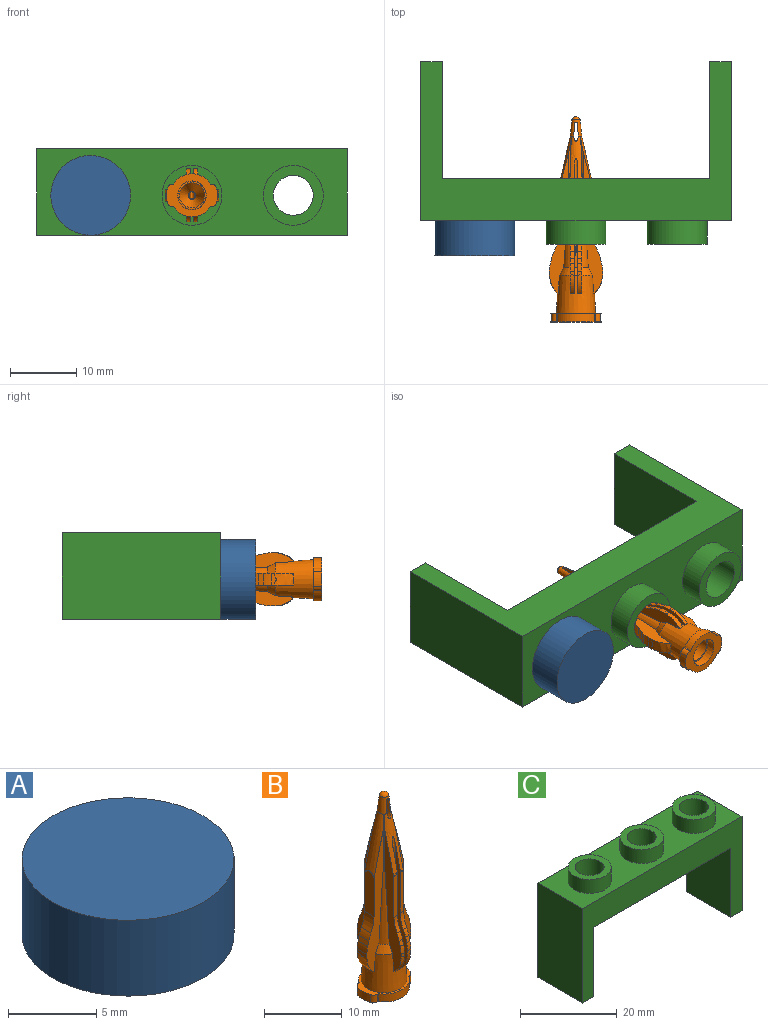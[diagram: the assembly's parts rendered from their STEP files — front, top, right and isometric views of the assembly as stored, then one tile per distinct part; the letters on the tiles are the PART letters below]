
ASSEMBLY  parts=3 mates=2
PART A: 3 faces, bbox 12x12x5.3 mm
  f0: cylinder r=6mm len=12mm, axis (0,0,-1), area 197.9mm2, adj f1,f2
  f1: plane 12x12mm, normal (0,0,1), area 113.1mm2, adj f0
  f2: plane 12x12mm, normal (0,0,-1), area 113.1mm2, adj f0
PART B: 130 faces, bbox 8.4x8.4x31.3 mm
  f0: cone r=0.52mm half-angle=51deg, axis (0,0,-1), area 0mm2, adj f12,f128
  f1: cone r=0.38mm half-angle=6deg, axis (0,0,-1), area 9.4mm2, adj f2,f5,f8,f34,f114,f115,f116,f117
  f2: cone r=3.2mm half-angle=12.5deg, axis (0,0,-1), area 12.4mm2, adj f1,f3,f4,f46,f47,f79,f82,f85
  f3: plane 19.1x2.13mm, normal (-1,-0.02,0), area 16.3mm2, adj f2,f55,f56,f57,f58,f82,f83,f95
  f4: plane 19.1x2.13mm, normal (1,-0.02,0), area 16.3mm2, adj f2,f51,f52,f53,f54,f81,f82,f95
  f5: cone r=0.87mm half-angle=12.5deg, axis (0,0,-1), area 12.4mm2, adj f1,f6,f7,f49,f50,f67,f70,f97
  f6: plane 19.1x2.13mm, normal (1,0.02,0), area 16.3mm2, adj f5,f91,f92,f93,f94,f95,f96,f97
  f7: plane 19.1x2.13mm, normal (-1,0.02,0), area 16.3mm2, adj f5,f86,f87,f88,f89,f90,f95,f97
  f8: cone r=0.87mm half-angle=12.6deg, axis (0,0,-1), area 16.6mm2, adj f1,f9,f39,f43,f72,f123
  f9: plane 21.7x3.25mm, normal (0,-1,0), area 26.6mm2, adj f8,f40,f41,f42,f43,f44,f75,f76
  f10: cone r=0.6mm half-angle=24.1deg, axis (0,0,-1), area 25mm2, adj f11,f15
  f11: cylinder r=0.6mm len=13.21mm, axis (0,0,1), area 49.8mm2, adj f10,f12
  f12: cone r=0.52mm half-angle=1deg, axis (0,0,-1), area 16.2mm2, adj f0,f11,f13,f125,f126
  f13: cone r=0.52mm half-angle=51deg, axis (0,0,-1), area 0mm2, adj f12,f127
  f14: plane 4.24x4.24mm, normal (0,0,-1), area 2.8mm2, adj f15,f28
  f15: cylinder r=1.9mm len=5.75mm, axis (0,0,1), area 68.6mm2, adj f10,f14
  f16: plane 1.25x0.12mm, normal (0,-1,0), area 0.1mm2, adj f17,f27,f29,f59
  f17: cylinder r=0.8mm len=1.25mm, axis (0,0,-1), area 1.3mm2, adj f16,f18,f27,f59
  f18: cylinder r=3.82mm len=2.28mm, axis (0,0,-1), area 2.9mm2, adj f17,f19,f27,f59
  f19: cylinder r=0.8mm len=1.25mm, axis (0,0,-1), area 1.3mm2, adj f18,f20,f27,f59
  f20: plane 1.25x0.12mm, normal (0,1,0), area 0.1mm2, adj f19,f21,f27,f59
  f21: cylinder r=3.25mm len=5.54mm, axis (0,0,1), area 8.3mm2, adj f20,f22,f27,f59
  f22: plane 1.25x0.12mm, normal (0,1,0), area 0.1mm2, adj f21,f23,f27,f59
  f23: cylinder r=0.8mm len=1.25mm, axis (0,0,-1), area 1.3mm2, adj f22,f24,f27,f59
  f24: cylinder r=3.82mm len=2.28mm, axis (0,0,-1), area 2.9mm2, adj f23,f25,f27,f59
  f25: cylinder r=0.8mm len=1.25mm, axis (0,0,-1), area 1.3mm2, adj f24,f26,f27,f59
  f26: plane 1.25x0.12mm, normal (0,-1,0), area 0.1mm2, adj f25,f27,f29,f59
  f27: plane 7.65x6.5mm, normal (0,0,-1), area 22.3mm2, adj f16,f17,f18,f19,f20,f21,f22,f23
  f28: cone r=1.9mm half-angle=2.2deg, axis (0,0,-1), area 16.9mm2, adj f14,f27
  f29: cylinder r=3.25mm len=5.54mm, axis (0,0,1), area 8.3mm2, adj f16,f26,f27,f59
  f30: plane 8.53x0.39mm, normal (-0.64,-0.77,0), area 1.6mm2, adj f34,f61,f114
  f31: plane 1.77x0.74mm, normal (0.97,0,0.24), area 1.3mm2, adj f61,f65,f110,f111
  f32: cylinder r=5mm len=2.29mm, axis (0,1,0), area 4.2mm2, adj f33,f61,f65,f111
  f33: plane 6.76x1.77mm, normal (1,0,0), area 11.5mm2, adj f32,f61,f65,f122
  f34: cone r=3.2mm half-angle=12.6deg, axis (0,0,-1), area 16.6mm2, adj f1,f30,f35,f61,f65,f122
  f35: plane 8.53x0.39mm, normal (-0.64,0.77,0), area 1.6mm2, adj f34,f65,f117
  f36: plane 1.77x0.73mm, normal (1,0,0), area 1mm2, adj f61,f63,f65,f110
  f37: plane 0.04x0.02mm, normal (0,-0.93,-0.37), area 0mm2, adj f66,f67,f117
  f38: plane 0.04x0.02mm, normal (0,-0.93,-0.37), area 0mm2, adj f70,f71,f116
  f39: plane 8.53x0.39mm, normal (0.64,0.77,0), area 1.6mm2, adj f8,f72,f116
  f40: plane 1.77x0.74mm, normal (-0.97,0,0.24), area 1.3mm2, adj f9,f72,f108,f109
  f41: cylinder r=5mm len=2.29mm, axis (0,-1,0), area 4.2mm2, adj f9,f42,f72,f109
  f42: plane 6.76x1.77mm, normal (-1,0,0), area 11.5mm2, adj f9,f41,f72,f123
  f43: plane 8.53x0.39mm, normal (0.64,-0.77,0), area 1.6mm2, adj f8,f9,f115
  f44: plane 1.77x0.73mm, normal (-1,0,0), area 1mm2, adj f9,f72,f75,f108
  f45: plane 0.04x0.02mm, normal (0,0.93,-0.37), area 0mm2, adj f78,f79,f115
  f46: plane 8.53x0.39mm, normal (-0.77,0.64,0), area 1.6mm2, adj f2,f79,f115
  f47: plane 8.53x0.39mm, normal (0.77,0.64,0), area 1.6mm2, adj f2,f85,f114
  f48: plane 0.04x0.02mm, normal (0,0.93,-0.37), area 0mm2, adj f60,f85,f114
  f49: plane 8.53x0.39mm, normal (0.77,-0.64,0), area 1.6mm2, adj f5,f67,f117
  f50: plane 8.53x0.39mm, normal (-0.77,-0.64,0), area 1.6mm2, adj f5,f70,f116
  f51: plane 0.67x0.6mm, normal (0,-1,0), area 0.3mm2, adj f4,f79,f81,f102
  f52: plane 0.74x0.61mm, normal (0,-0.97,0.24), area 0.5mm2, adj f4,f79,f102,f103
  f53: cylinder r=5mm len=2.29mm, axis (1,0,0), area 1.5mm2, adj f4,f54,f79,f103
  f54: plane 6.68x0.62mm, normal (0,-1,0), area 4mm2, adj f4,f53,f79,f119
  f55: plane 6.68x0.62mm, normal (0,-1,0), area 4mm2, adj f3,f56,f85,f118
  f56: cylinder r=5mm len=2.29mm, axis (1,0,0), area 1.5mm2, adj f3,f55,f85,f106
  f57: plane 0.74x0.61mm, normal (0,-0.97,0.24), area 0.5mm2, adj f3,f85,f106,f107
  f58: plane 0.67x0.6mm, normal (0,-1,0), area 0.3mm2, adj f3,f83,f85,f107
  f59: plane 7.65x6.5mm, normal (0,0,1), area 9.7mm2, adj f16,f17,f18,f19,f20,f21,f22,f23
  f60: cone r=2.63mm half-angle=25.5deg, axis (0,0,-1), area 2.5mm2, adj f48,f61,f85,f95,f114
  f61: plane 21.7x3.25mm, normal (0,-1,0), area 26.7mm2, adj f30,f31,f32,f33,f34,f36,f60,f62
  f62: plane 0.52x0.24mm, normal (-0.98,0,-0.18), area 0mm2, adj f61,f63,f95
  f63: bspline ~4.99x3.09mm, area 5.6mm2, adj f36,f61,f62,f64,f65,f95
  f64: plane 0.52x0.24mm, normal (-0.98,0,-0.18), area 0mm2, adj f63,f65,f95
  f65: plane 21.7x3.25mm, normal (0,1,0), area 26.7mm2, adj f31,f32,f33,f34,f35,f36,f63,f64
  f66: cone r=2.63mm half-angle=25.5deg, axis (0,0,-1), area 2.5mm2, adj f37,f65,f67,f95,f117
  f67: plane 21.42x2.98mm, normal (1,0,0), area 26.7mm2, adj f5,f37,f49,f66,f68,f86,f87,f88
  f68: plane 1.1x0.27mm, normal (0,-0.99,-0.12), area 0.1mm2, adj f67,f86,f95
  f69: plane 1.1x0.27mm, normal (0,-0.99,-0.12), area 0.1mm2, adj f70,f95,f96
  f70: plane 21.42x2.98mm, normal (-1,0,0), area 26.7mm2, adj f5,f38,f50,f69,f71,f91,f92,f93
  f71: cone r=2.63mm half-angle=25.5deg, axis (0,0,-1), area 2.5mm2, adj f38,f70,f72,f95,f116
  f72: plane 21.7x3.25mm, normal (0,1,0), area 26.6mm2, adj f8,f39,f40,f41,f42,f44,f71,f73
  f73: plane 0.06x0.04mm, normal (0.88,0,-0.47), area 0mm2, adj f72,f74,f95
  f74: plane 2.29x0.21mm, normal (1,0,-0.08), area 0.3mm2, adj f72,f73,f75,f95
  f75: bspline ~4.99x3.09mm, area 5.6mm2, adj f9,f44,f72,f74,f76,f95
  f76: plane 2.29x0.21mm, normal (1,0,-0.08), area 0.3mm2, adj f9,f75,f77,f95
  f77: plane 0.06x0.04mm, normal (0.88,0,-0.47), area 0mm2, adj f9,f76,f95
  f78: cone r=2.63mm half-angle=25.5deg, axis (0,0,-1), area 2.5mm2, adj f9,f45,f79,f95,f115
  f79: plane 21.42x2.98mm, normal (-1,0,0), area 26.7mm2, adj f2,f45,f46,f51,f52,f53,f54,f78
  f80: plane 1.1x0.27mm, normal (0,0.99,-0.12), area 0.1mm2, adj f79,f81,f95
  f81: bspline ~3.08x2.76mm, area 2mm2, adj f4,f51,f79,f80,f95
  f82: bspline ~23.75x0.91mm, area 11.2mm2, adj f2,f3,f4,f99,f112
  f83: bspline ~3.08x2.76mm, area 2mm2, adj f3,f58,f84,f85,f95
  f84: plane 1.1x0.27mm, normal (0,0.99,-0.12), area 0.1mm2, adj f83,f85,f95
  f85: plane 21.42x2.98mm, normal (1,0,0), area 26.7mm2, adj f2,f47,f48,f55,f56,f57,f58,f60
  f86: bspline ~3.08x2.76mm, area 2mm2, adj f7,f67,f68,f87,f95
  f87: plane 0.67x0.6mm, normal (0,1,0), area 0.3mm2, adj f7,f67,f86,f104
  f88: plane 0.74x0.61mm, normal (0,0.97,0.24), area 0.5mm2, adj f7,f67,f104,f105
  f89: cylinder r=5mm len=2.29mm, axis (-1,0,0), area 1.5mm2, adj f7,f67,f90,f105
  f90: plane 6.68x0.62mm, normal (0,1,0), area 4mm2, adj f7,f67,f89,f121
  f91: plane 6.68x0.62mm, normal (0,1,0), area 4mm2, adj f6,f70,f92,f120
  f92: cylinder r=5mm len=2.29mm, axis (-1,0,0), area 1.5mm2, adj f6,f70,f91,f101
  f93: plane 0.74x0.61mm, normal (0,0.97,0.24), area 0.5mm2, adj f6,f70,f100,f101
  f94: plane 0.67x0.6mm, normal (0,1,0), area 0.3mm2, adj f6,f70,f96,f100
  f95: cone r=2.63mm half-angle=3.2deg, axis (0,0,-1), area 85.1mm2, adj f3,f4,f6,f7,f9,f59,f60,f61
  f96: bspline ~3.08x2.76mm, area 2mm2, adj f6,f69,f70,f94,f95
  f97: bspline ~23.75x0.91mm, area 11.2mm2, adj f5,f6,f7,f98,f113
  f98: cone r=1.14mm half-angle=26.4deg, axis (0,0,-1), area 0.7mm2, adj f6,f7,f95,f97,f113
  f99: cone r=1.14mm half-angle=26.4deg, axis (0,0,-1), area 0.7mm2, adj f3,f4,f82,f95,f112
  f100: cylinder r=5mm len=1.21mm, axis (-1,0,0), area 0.7mm2, adj f6,f70,f93,f94
  f101: cylinder r=5mm len=1.08mm, axis (-1,0,0), area 0.7mm2, adj f6,f70,f92,f93
  f102: cylinder r=5mm len=1.21mm, axis (1,0,0), area 0.7mm2, adj f4,f51,f52,f79
  f103: cylinder r=5mm len=1.08mm, axis (1,0,0), area 0.7mm2, adj f4,f52,f53,f79
  f104: cylinder r=5mm len=1.21mm, axis (-1,0,0), area 0.7mm2, adj f7,f67,f87,f88
  f105: cylinder r=5mm len=1.08mm, axis (-1,0,0), area 0.7mm2, adj f7,f67,f88,f89
  f106: cylinder r=5mm len=1.08mm, axis (1,0,0), area 0.7mm2, adj f3,f56,f57,f85
  f107: cylinder r=5mm len=1.21mm, axis (1,0,0), area 0.7mm2, adj f3,f57,f58,f85
  f108: cylinder r=5mm len=1.77mm, axis (0,1,0), area 2.2mm2, adj f9,f40,f44,f72
  f109: cylinder r=5mm len=1.77mm, axis (0,-1,0), area 2.1mm2, adj f9,f40,f41,f72
  f110: cylinder r=5mm len=1.77mm, axis (0,1,0), area 2.2mm2, adj f31,f36,f61,f65
  f111: cylinder r=5mm len=1.77mm, axis (0,1,0), area 2.1mm2, adj f31,f32,f61,f65
  f112: cone r=0.87mm half-angle=3.4deg, axis (0,0,-1), area 1.2mm2, adj f82,f99
  f113: cone r=0.87mm half-angle=3.4deg, axis (0,0,-1), area 1.2mm2, adj f97,f98
  f114: cone r=0.87mm half-angle=3.4deg, axis (0,0,-1), area 10.9mm2, adj f1,f30,f47,f48,f60,f61,f85
  f115: cone r=0.87mm half-angle=3.4deg, axis (0,0,-1), area 10.9mm2, adj f1,f9,f43,f45,f46,f78,f79
  f116: cone r=0.87mm half-angle=3.4deg, axis (0,0,-1), area 10.9mm2, adj f1,f38,f39,f50,f70,f71,f72
  f117: cone r=0.87mm half-angle=3.4deg, axis (0,0,-1), area 10.9mm2, adj f1,f35,f37,f49,f65,f66,f67
  f118: bspline ~0.9x0.89mm, area 0.1mm2, adj f2,f3,f55,f85
  f119: bspline ~0.9x0.89mm, area 0.1mm2, adj f2,f4,f54,f79
  f120: bspline ~0.9x0.89mm, area 0.1mm2, adj f5,f6,f70,f91
  f121: bspline ~0.94x0.93mm, area 0.1mm2, adj f5,f7,f67,f90
  f122: bspline ~2.25x1mm, area 0.2mm2, adj f33,f34,f61,f65
  f123: bspline ~2.25x1mm, area 0.2mm2, adj f8,f9,f42,f72
  f124: sphere r=0.66mm, area 1.7mm2, adj f1
  f125: extruded ~0.8x0.73mm, area 1mm2, adj f5,f12,f127,f128
  f126: extruded ~0.8x0.73mm, area 1mm2, adj f2,f12,f127,f128
  f127: plane 2.36x1.99mm, normal (0.99,0,-0.1), area 2.7mm2, adj f1,f13,f125,f126,f129
  f128: plane 2.36x1.99mm, normal (-0.99,0,-0.1), area 2.7mm2, adj f0,f1,f125,f126,f129
  f129: cylinder r=0.17mm len=1.29mm, axis (0,-1,0), area 0.6mm2, adj f1,f127,f128
PART C: 19 faces, bbox 46.7x13x27.4 mm
  f0: plane 46.75x23.89mm, normal (0,1,0), area 412mm2, adj f1,f2,f3,f4,f5,f7,f17,f18
  f1: plane 23.89x13mm, normal (-1,0,0), area 310.6mm2, adj f0,f6,f7,f18
  f2: plane 23.89x13mm, normal (1,0,0), area 310.6mm2, adj f0,f6,f7,f17
  f3: plane 17.53x13mm, normal (1,0,0), area 227.8mm2, adj f0,f5,f6,f18
  f4: plane 17.53x13mm, normal (-1,0,0), area 227.8mm2, adj f0,f5,f6,f17
  f5: plane 40.23x13mm, normal (0,0,-1), area 438.4mm2, adj f0,f3,f4,f6,f8,f11,f14
  f6: plane 46.75x23.89mm, normal (0,-1,0), area 412mm2, adj f1,f2,f3,f4,f5,f7,f17,f18
  f7: plane 46.75x13mm, normal (0,0,1), area 417.5mm2, adj f0,f1,f2,f6,f9,f12,f15
  f8: cylinder r=2.98mm len=9.86mm, axis (0,0,-1), area 184.4mm2, adj f5,f10
  f9: cylinder r=4.47mm len=8.95mm, axis (0,0,-1), area 98.2mm2, adj f7,f10
  f10: plane 8.95x8.95mm, normal (0,0,1), area 35.1mm2, adj f8,f9
  f11: cylinder r=3mm len=9.86mm, axis (0,0,-1), area 186.1mm2, adj f5,f13
  f12: cylinder r=4.5mm len=9mm, axis (0,0,-1), area 98.8mm2, adj f7,f13
  f13: plane 9x9mm, normal (0,0,1), area 35.3mm2, adj f11,f12
  f14: cylinder r=3mm len=9.86mm, axis (0,0,-1), area 186.1mm2, adj f5,f16
  f15: cylinder r=4.5mm len=9mm, axis (0,0,-1), area 98.8mm2, adj f7,f16
  f16: plane 9x9mm, normal (0,0,1), area 35.3mm2, adj f14,f15
  f17: plane 13x3.26mm, normal (0,0,-1), area 42.4mm2, adj f0,f2,f4,f6
  f18: plane 13x3.26mm, normal (0,0,-1), area 42.4mm2, adj f0,f1,f3,f6
PLACE A rot(axis=(1,0,0),90deg) t=(-21.38,-28.01,9.99)mm
PLACE B rot(axis=(-1,0,0),90deg) t=(-6.14,-43.23,9.99)mm
PLACE C rot(axis=(1,0,0),90deg) t=(-3.36,0,-16.01)mm fixed
MATE fastened A.f0 <-> C.f8  axis (0,1,0) through (-21.38,-28.01,9.99)mm
MATE slider B.f28 <-> C.f11  axis (0,-1,0) through (-6.14,-43.23,9.99)mm
